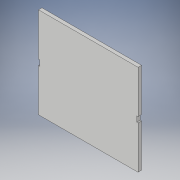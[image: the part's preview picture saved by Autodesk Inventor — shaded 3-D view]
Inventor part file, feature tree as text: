
AUTODESK INVENTOR PART (.ipt)
format: ipt  version: 2018 (Build 220112000, 112)  size: 101,888 bytes
history: native  units: in
note: dims shown in document units (in); Inventor stores cm internally (conversion verified against a paired STEP export)
features: extrude x1, sketch x1
ambient origin geometry x8: Origin, YZ Plane, XZ Plane, XY Plane, X Axis, Y Axis, Z Axis, Center Point
bodies: Solid1 (feature_tree)
feature tree (2):
  extrude  "Extrusion1"  Depth=26.086in
  sketch  "Sketch1"  dims[d0=28.583in d1=26.086in d2=0.7875in d3=1.575in d4=0.369in d5=1.0in d6=0.0in]
